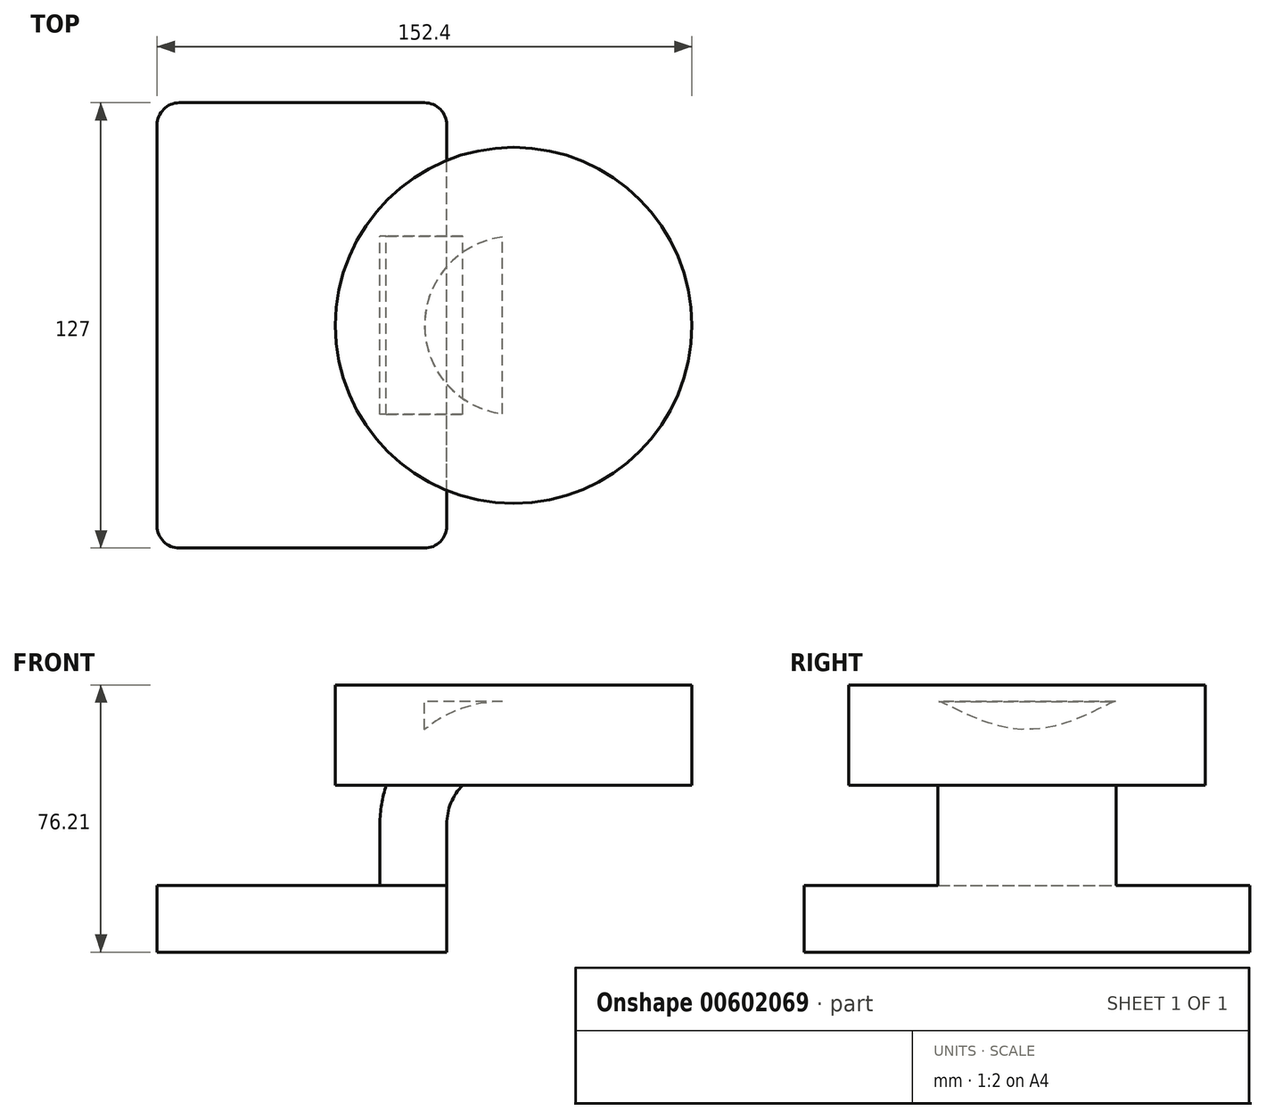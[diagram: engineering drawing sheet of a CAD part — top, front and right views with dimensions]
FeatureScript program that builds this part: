
annotation { "Feature Type Name" : "Feature", "Feature Type Description" : "" }
export const myFeature = defineFeature(function(context is Context, id is Id, definition is map)
    precondition{}
    {
        {
            var Q0;
            Q0=qCreatedBy(makeId("Front.planeOp"),FACE);
            var sketch = newSketch(context, id + "F0", { "sketchPlane" : qUnion([Q0])});
            skLineSegment(sketch, "E0.bottom", {"start": v(41.28, 9.53) * mm, "end": v(-41.28, 9.53) * mm});
            skLineSegment(sketch, "E0.top", {"start": v(41.28, -9.52) * mm, "end": v(-41.27, -9.52) * mm});
            skLineSegment(sketch, "E0.left", {"start": v(41.28, 9.53) * mm, "end": v(41.28, -9.52) * mm});
            skLineSegment(sketch, "E0.right", {"start": v(-41.28, 9.53) * mm, "end": v(-41.27, -9.52) * mm});
            skPoint(sketch, "E0.middle", {"position": v(0, 0) * mm});
            skLineSegment(sketch, "E1.bottom", {"start": v(111.12, 66.68) * mm, "end": v(60.33, 66.68) * mm});
            skLineSegment(sketch, "E1.top", {"start": v(111.12, 38.1) * mm, "end": v(60.33, 38.1) * mm});
            skLineSegment(sketch, "E1.left", {"start": v(111.12, 66.68) * mm, "end": v(111.12, 38.1) * mm});
            skLineSegment(sketch, "E1.right", {"start": v(60.33, 66.68) * mm, "end": v(60.33, 38.1) * mm});
            skPoint(sketch, "E1.middle", {"position": v(85.72, 52.39) * mm});
            skLineSegment(sketch, "E2", {"start": v(41.27, 9.53) * mm, "end": v(41.27, 27) * mm});
            skArc(sketch, "E3", {"start": v(41.27, 27) * mm, "mid": v(45.92, 38.23) * mm, "end": v(57.15, 42.88) * mm});
            skLineSegment(sketch, "E4", {"start": v(57.15, 42.88) * mm, "end": v(85.72, 42.88) * mm});
            skLineSegment(sketch, "E5.0", {"start": v(57.15, 61.93) * mm, "end": v(85.72, 61.93) * mm});
            skArc(sketch, "E5.1", {"start": v(22.23, 27) * mm, "mid": v(32.45, 51.7) * mm, "end": v(57.15, 61.93) * mm});
            skLineSegment(sketch, "E5.2", {"start": v(22.22, 9.53) * mm, "end": v(22.22, 27) * mm});
            skLineSegment(sketch, "E6", {"start": v(85.72, 42.88) * mm, "end": v(85.72, 61.93) * mm});
            skFitSpline(sketch, "E7", {"points": [v(-41.28, 9.53) * mm, v(57.15, 61.93) * mm], "startDerivative": vector(48.7, 106.07) * mm, "endDerivative": vector(109.55, -0.52) * mm});
            skSolve(sketch);
        }
        {
            var Q0;
            Q0=makeQuery(id+"F0.imprint","IMPRINT",FACE,{"disambiguationData":[TD([[makeQuery(id+"F0.imprint","IMPRINT",EDGE,{"derivedFrom":sQuery(id+"F0.wireOp",EDGE,"E0.top")}),-1.0]])]});
            extrude(context, id + "F1", {"entities" : qUnion([Q0]), "endBound" : BoundingType.SYMMETRIC, "depth" : 127 * mm, "offsetDistance" : 25.4 * mm});
        }
        {
            var Q0;
            {var subQ1=sQuery(id+"F0.wireOp",EDGE,"E2");Q0=makeQuery(id+"F0.imprint","IMPRINT",FACE,{"disambiguationData":[TD([[makeQuery(id+"F0.imprint","IMPRINT",EDGE,{"derivedFrom":subQ1}),1.0]])]});}
            var Q1;
            {var subQ5=sQuery(id+"F0.wireOp",EDGE,"E6");Q1=makeQuery(id+"F0.imprint","IMPRINT",FACE,{"disambiguationData":[TD([[makeQuery(id+"F0.imprint","IMPRINT",EDGE,{"derivedFrom":subQ5}),1.0]])]});}
            extrude(context, id + "F2", {"entities" : qUnion([Q0, Q1]), "operationType" : NewBodyOperationType.ADD, "endBound" : BoundingType.SYMMETRIC, "depth" : 50.8 * mm, "offsetDistance" : 25.4 * mm});
        }
        {
            var Q0;
            Q0=makeQuery(id+"F0.imprint","IMPRINT",FACE,{"disambiguationData":[TD([[makeQuery(id+"F0.imprint","IMPRINT",EDGE,{"derivedFrom":sQuery(id+"F0.wireOp",EDGE,"E5.1")}),1.0]])]});
            extrude(context, id + "F3", {"entities" : qUnion([Q0]), "operationType" : NewBodyOperationType.ADD, "endBound" : BoundingType.SYMMETRIC, "depth" : 15.88 * mm, "offsetDistance" : 25.4 * mm});
        }
        {
            var Q0;
            {var subQ1=sQuery(id+"F0.wireOp",EDGE,"E1.bottom");Q0=makeQuery(id+"F0.imprint","IMPRINT",FACE,{"disambiguationData":[TD([[makeQuery(id+"F0.imprint","IMPRINT",EDGE,{"derivedFrom":subQ1}),1.0]])]});}
            var Q1;
            Q1=sQuery(id+"F0.wireOp",EDGE,"E1.right");
            revolve(context, id + "F4", {"operationType" : NewBodyOperationType.ADD, "entities" : qUnion([Q0]), "axis" : qUnion([Q1]), "revolveType" : RevolveType.FULL});
        }
        {
            var Q0;
            Q0=makeQuery(id+"F1.opExtrude","CAP_EDGE",EDGE,{"disambiguationData":[OSD([sQuery(id+"F0.wireOp",EDGE,"E0.left")])],"isStart":false});
            var Q1;
            Q1=makeQuery(id+"F1.opExtrude","CAP_EDGE",EDGE,{"disambiguationData":[OSD([sQuery(id+"F0.wireOp",EDGE,"E0.right")])],"isStart":false});
            var Q2;
            Q2=makeQuery(id+"F1.opExtrude","CAP_EDGE",EDGE,{"disambiguationData":[OSD([sQuery(id+"F0.wireOp",EDGE,"E0.right")])],"isStart":true});
            var Q3;
            Q3=makeQuery(id+"F1.opExtrude","CAP_EDGE",EDGE,{"disambiguationData":[OSD([sQuery(id+"F0.wireOp",EDGE,"E0.left")])],"isStart":true});
            fillet(context, id + "F5", {"entities" : qUnion([Q0, Q1, Q2, Q3]), "radius" : 6.35 * mm, "tangentPropagation" : true, "allowEdgeOverflow" : false});
        }
    });
